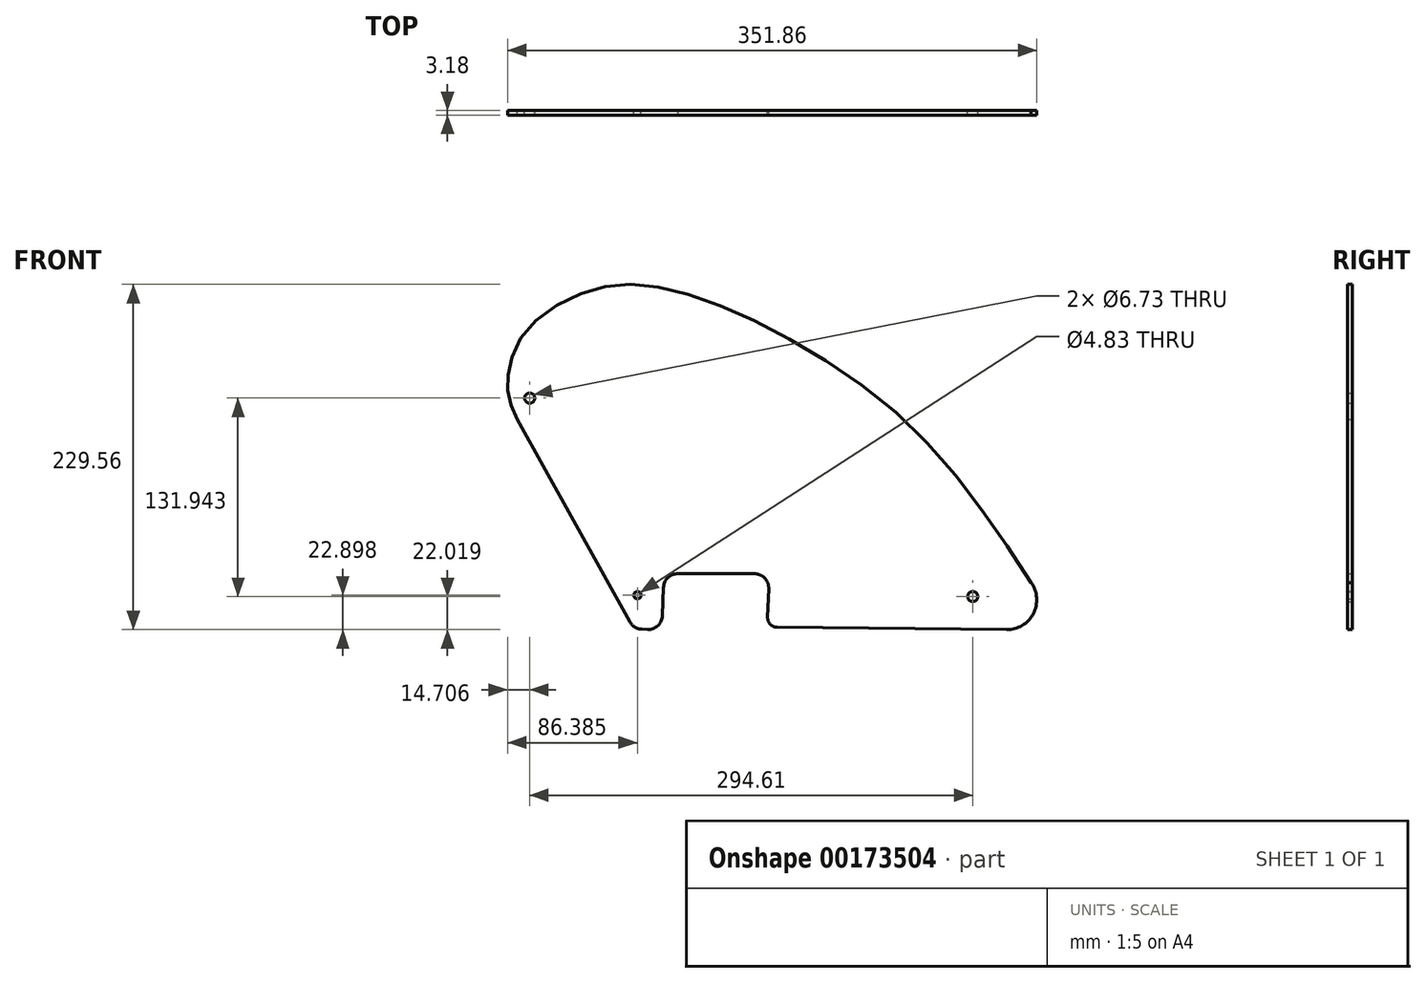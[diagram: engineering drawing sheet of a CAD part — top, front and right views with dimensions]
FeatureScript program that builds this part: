
annotation { "Feature Type Name" : "Feature", "Feature Type Description" : "" }
export const myFeature = defineFeature(function(context is Context, id is Id, definition is map)
    precondition{}
    {
        {
            var Q0;
            Q0=qCreatedBy(makeId("Front.planeOp"),FACE);
            var sketch = newSketch(context, id + "F0", { "sketchPlane" : qUnion([Q0])});
            skLineSegment(sketch, "E0", {"start": v(-4.14, -125.76) * mm, "end": v(-0.33, -125.9) * mm});
            skLineSegment(sketch, "E1", {"start": v(9.53, -116.73) * mm, "end": v(10.22, -98.02) * mm});
            skLineSegment(sketch, "E2", {"start": v(85.77, -124.5) * mm, "end": v(238.43, -126.05) * mm});
            skLineSegment(sketch, "E3", {"start": v(-12.12, -120.87) * mm, "end": v(-86.97, 13.77) * mm});
            skCircle(sketch, "E4", {"center": v(-7.07, -103.15) * mm, "radius": 2.41 * mm});
            skPoint(sketch, "E5.visualSharp", {"position": v(-9.5, -125.57) * mm});
            skArc(sketch, "E5.filletArc", {"start": v(-12.12, -120.87) * mm, "mid": v(-8.77, -124.36) * mm, "end": v(-4.14, -125.76) * mm});
            skArc(sketch, "E6.filletArc", {"start": v(-0.33, -125.9) * mm, "mid": v(6.5, -123.36) * mm, "end": v(9.53, -116.73) * mm});
            skArc(sketch, "E7.filletArc", {"start": v(20.09, -88.85) * mm, "mid": v(13.25, -91.39) * mm, "end": v(10.22, -98.02) * mm});
            skFitSpline(sketch, "E8", {"points": [v(254.66, -94.73) * mm, v(174.67, 9.25) * mm, v(71.7, 78.77) * mm, v(-1.13, 102.88) * mm, v(-46.17, 96.85) * mm, v(-82.4, 71.07) * mm, v(-92.68, 45.74) * mm, v(-92.7, 29.38) * mm, v(-86.97, 13.77) * mm], "startDerivative": vector(-367.82, 560.42) * mm, "endDerivative": vector(99.03, -222.32) * mm});
            skLineSegment(sketch, "E9.0", {"start": v(80.2, -98.72) * mm, "end": v(79.49, -117.92) * mm});
            skLineSegment(sketch, "E10", {"start": v(-7.07, -103.15) * mm, "end": v(-7.07, -45.78) * mm, "construction": true});
            skLineSegment(sketch, "E11", {"start": v(-7.07, -103.15) * mm, "end": v(-29.32, -103.15) * mm, "construction": true});
            skCircle(sketch, "E12", {"center": v(-78.75, 27.91) * mm, "radius": 3.37 * mm});
            skCircle(sketch, "E13", {"center": v(215.86, -104.03) * mm, "radius": 3.37 * mm});
            skLineSegment(sketch, "E14", {"start": v(20.09, -88.85) * mm, "end": v(70.67, -88.85) * mm});
            skPoint(sketch, "E15.visualSharp", {"position": v(80.55, -88.85) * mm});
            skArc(sketch, "E15.filletArc", {"start": v(80.2, -98.72) * mm, "mid": v(77.53, -91.76) * mm, "end": v(70.67, -88.85) * mm});
            skArc(sketch, "E16.filletArc", {"start": v(79.49, -117.92) * mm, "mid": v(81.24, -122.53) * mm, "end": v(85.77, -124.5) * mm});
            skArc(sketch, "E17", {"start": v(238.43, -126.05) * mm, "mid": v(256.18, -115.38) * mm, "end": v(254.66, -94.73) * mm});
            skLineSegment(sketch, "E18", {"start": v(-93.42, 35.29) * mm, "end": v(-92.7, -177.02) * mm, "construction": true});
            skLineSegment(sketch, "E19", {"start": v(258.4, -105.86) * mm, "end": v(259.9, -175.69) * mm, "construction": true});
            skSolve(sketch);
        }
        {
            var Q0;
            Q0 = qSketchRegion(id + "F0", true);
            extrude(context, id + "F1", {"entities" : qUnion([Q0]), "depth" : 3.17 * mm});
        }
        {
            var Q0;
            Q0 = qSketchRegion(id + "F0", true);
            extrude(context, id + "F2", {"entities" : qUnion([Q0]), "operationType" : NewBodyOperationType.ADD, "depth" : 3.17 * mm});
        }
    });
